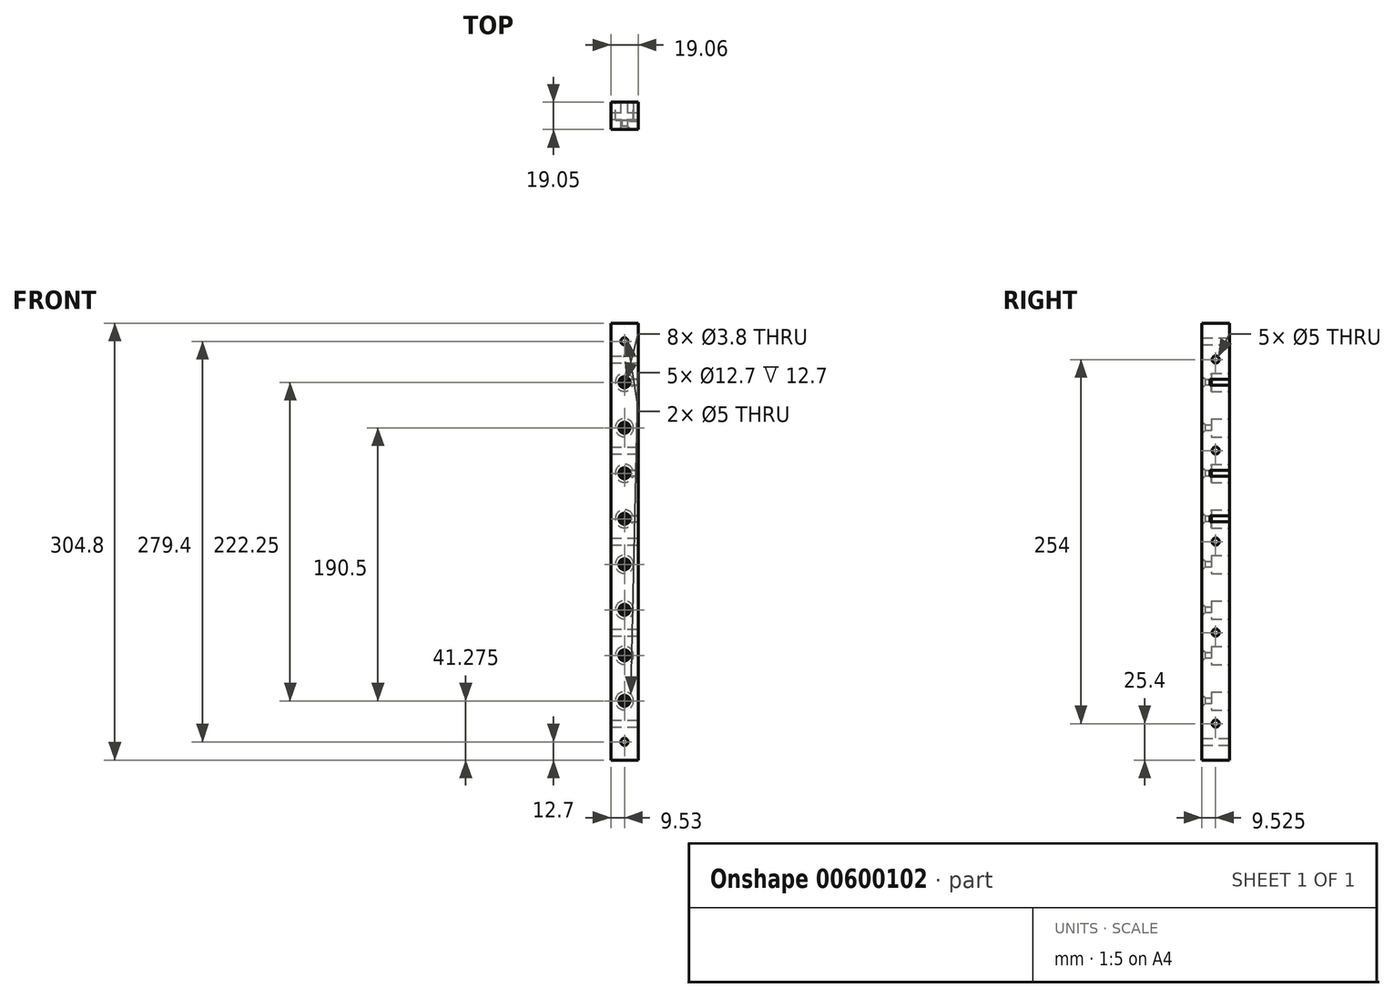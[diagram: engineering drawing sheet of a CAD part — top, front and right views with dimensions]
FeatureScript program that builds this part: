
annotation { "Feature Type Name" : "Feature", "Feature Type Description" : "" }
export const myFeature = defineFeature(function(context is Context, id is Id, definition is map)
    precondition{}
    {
        {
            var Q0;
            Q0=qCreatedBy(makeId("Front.planeOp"),FACE);
            var sketch = newSketch(context, id + "F0", { "sketchPlane" : qUnion([Q0])});
            skLineSegment(sketch, "E0.bottom", {"start": v(-9.52, 152.4) * mm, "end": v(9.53, 152.4) * mm});
            skLineSegment(sketch, "E0.top", {"start": v(-9.53, -152.4) * mm, "end": v(9.52, -152.4) * mm});
            skLineSegment(sketch, "E0.left", {"start": v(-9.52, 152.4) * mm, "end": v(-9.53, -152.4) * mm});
            skLineSegment(sketch, "E0.right", {"start": v(9.53, 152.4) * mm, "end": v(9.52, -152.4) * mm});
            skPoint(sketch, "E0.middle", {"position": v(0, 0) * mm});
            skPoint(sketch, "E1", {"position": v(0, 15.88) * mm});
            skPoint(sketch, "E2", {"position": v(0, -15.88) * mm});
            skPoint(sketch, "E3", {"position": v(0, -47.62) * mm});
            skPoint(sketch, "E4", {"position": v(0, -79.38) * mm});
            skPoint(sketch, "E5", {"position": v(0, -111.12) * mm});
            skPoint(sketch, "E6", {"position": v(0, 47.62) * mm});
            skPoint(sketch, "E7", {"position": v(0, 79.38) * mm});
            skPoint(sketch, "E8", {"position": v(0, 111.12) * mm});
            skSolve(sketch);
        }
        {
            var Q0;
            Q0=makeQuery(id+"F0.imprint","IMPRINT",FACE,{"disambiguationData":[TD([[makeQuery(id+"F0.imprint","IMPRINT",EDGE,{"derivedFrom":sQuery(id+"F0.wireOp",EDGE,"E0.bottom")}),-1.0]])]});
            extrude(context, id + "F1", {"entities" : qUnion([Q0]), "oppositeDirection" : true, "depth" : 19.05 * mm, "offsetDistance" : 25.4 * mm});
        }
        {
            var Q0;
            Q0=makeQuery(id+"F1.opExtrude","SWEPT_FACE",FACE,{"disambiguationData":[OSD([sQuery(id+"F0.wireOp",EDGE,"E0.right")])]});
            var sketch = newSketch(context, id + "F2", { "sketchPlane" : qUnion([Q0])});
            skPoint(sketch, "E9", {"position": v(9.52, 0) * mm});
            skPoint(sketch, "E10", {"position": v(9.53, -63.5) * mm});
            skPoint(sketch, "E11", {"position": v(9.52, 63.5) * mm});
            skPoint(sketch, "E12", {"position": v(9.52, 127) * mm});
            skPoint(sketch, "E13", {"position": v(9.53, -127) * mm});
            skSolve(sketch);
        }
        {
            var Q0;
            Q0=sQuery(id+"F2.wireOp",VERTEX,"E12");
            var Q1;
            Q1=sQuery(id+"F2.wireOp",VERTEX,"E11");
            var Q2;
            Q2=sQuery(id+"F2.wireOp",VERTEX,"E9");
            var Q3;
            Q3=sQuery(id+"F2.wireOp",VERTEX,"E10");
            var Q4;
            Q4=sQuery(id+"F2.wireOp",VERTEX,"E13");
            var Q5;
            Q5=makeQuery(id+"F1.opExtrude","SWEPT_BODY",BODY,{"disambiguationData":[OSD([sQuery(id+"F0.wireOp",EDGE,"E0.bottom"),sQuery(id+"F0.wireOp",EDGE,"E0.top"),sQuery(id+"F0.wireOp",EDGE,"E0.left"),sQuery(id+"F0.wireOp",EDGE,"E0.right")])]});
            hole(context, id + "F3", {"style" : HoleStyle.SIMPLE, "endStyle" : HoleEndStyle.THROUGH, "standardTappedOrClearance" : lookupTablePath({ "standard" : "ISO", "engagement" : "75%", "pitch" : "1 mm", "size" : "M6", "type" : "Tapped" }), "standardBlindInLast" : lookupTablePath({ "standard" : "ISO", "engagement" : "75%", "pitch" : "1 mm", "size" : "M6", "type" : "Tapped" }), "holeDiameter" : 5 * mm, "majorDiameter" : 6 * mm, "showTappedDepth" : true, "isTappedThrough" : true, "tappedDepth" : 12.7 * mm, "tapClearance" : 3, "locations" : qUnion([Q0, Q1, Q2, Q3, Q4]), "scope" : qUnion([Q5])});
        }
        {
            var Q0;
            Q0=makeQuery(id+"F1.opExtrude","CAP_FACE",FACE,{"disambiguationData":[OSD([sQuery(id+"F0.wireOp",EDGE,"E0.bottom"),sQuery(id+"F0.wireOp",EDGE,"E0.top"),sQuery(id+"F0.wireOp",EDGE,"E0.left"),sQuery(id+"F0.wireOp",EDGE,"E0.right")])],"isStart":false});
            var sketch = newSketch(context, id + "F4", { "sketchPlane" : qUnion([Q0])});
            skPoint(sketch, "E14", {"position": v(0, 15.88) * mm});
            skPoint(sketch, "E15", {"position": v(0, 47.62) * mm});
            skPoint(sketch, "E16", {"position": v(0, 79.38) * mm});
            skPoint(sketch, "E17", {"position": v(0, 111.12) * mm});
            skPoint(sketch, "E18", {"position": v(0, -15.88) * mm});
            skPoint(sketch, "E19", {"position": v(0, -47.62) * mm});
            skPoint(sketch, "E20", {"position": v(0, -79.38) * mm});
            skPoint(sketch, "E21", {"position": v(0, -111.12) * mm});
            skCircle(sketch, "E22", {"center": v(0, 111.12) * mm, "radius": 6.35 * mm});
            skCircle(sketch, "E23", {"center": v(0, 79.38) * mm, "radius": 6.35 * mm});
            skCircle(sketch, "E24", {"center": v(0, 47.62) * mm, "radius": 6.35 * mm});
            skCircle(sketch, "E25", {"center": v(0, 15.88) * mm, "radius": 6.35 * mm});
            skCircle(sketch, "E26", {"center": v(0, -111.12) * mm, "radius": 6.35 * mm});
            skCircle(sketch, "E27", {"center": v(0, -79.38) * mm, "radius": 6.35 * mm});
            skCircle(sketch, "E28", {"center": v(0, -47.62) * mm, "radius": 6.35 * mm});
            skCircle(sketch, "E29", {"center": v(0, -15.88) * mm, "radius": 6.35 * mm});
            skSolve(sketch);
        }
        {
            var Q0;
            Q0=sQuery(id+"F0.wireOp",VERTEX,"E8");
            var Q1;
            Q1=sQuery(id+"F0.wireOp",VERTEX,"E7");
            var Q2;
            Q2=sQuery(id+"F0.wireOp",VERTEX,"E6");
            var Q3;
            Q3=sQuery(id+"F0.wireOp",VERTEX,"E1");
            var Q4;
            Q4=sQuery(id+"F0.wireOp",VERTEX,"E2");
            var Q5;
            Q5=sQuery(id+"F0.wireOp",VERTEX,"E3");
            var Q6;
            Q6=sQuery(id+"F0.wireOp",VERTEX,"E4");
            var Q7;
            Q7=sQuery(id+"F0.wireOp",VERTEX,"E5");
            var Q8;
            Q8=makeQuery(id+"F1.opExtrude","SWEPT_BODY",BODY,{"disambiguationData":[OSD([sQuery(id+"F0.wireOp",EDGE,"E0.bottom"),sQuery(id+"F0.wireOp",EDGE,"E0.top"),sQuery(id+"F0.wireOp",EDGE,"E0.left"),sQuery(id+"F0.wireOp",EDGE,"E0.right")])]});
            hole(context, id + "F5", {"style" : HoleStyle.C_SINK, "endStyle" : HoleEndStyle.BLIND, "standardTappedOrClearance" : lookupTablePath({ "standard" : "ANSI", "fit" : "Normal (ASME)", "size" : "#6", "type" : "Clearance" }), "standardBlindInLast" : lookupTablePath({ "fit" : "Free", "standard" : "ANSI", "size" : "#6", "type" : "Clearance" }), "holeDiameter" : 3.8 * mm, "cSinkDiameter" : 7.8 * mm, "cSinkAngle" : 82 * degree, "majorDiameter" : 6.35 * mm, "holeDepth" : 12.7 * mm, "isTappedThrough" : true, "tappedDepth" : 12.7 * mm, "tapClearance" : 3, "locations" : qUnion([Q0, Q1, Q2, Q3, Q4, Q5, Q6, Q7]), "scope" : qUnion([Q8])});
        }
        {
            var Q0;
            Q0=makeQuery(id+"F1.opExtrude","SWEPT_FACE",FACE,{"disambiguationData":[OSD([sQuery(id+"F0.wireOp",EDGE,"E0.right")])]});
            var sketch = newSketch(context, id + "F6", { "sketchPlane" : qUnion([Q0])});
            skPoint(sketch, "E30", {"position": v(19.05, 15.88) * mm});
            skLineSegment(sketch, "E31", {"start": v(5.72, 10.75) * mm, "end": v(5.72, 17.87) * mm});
            skLineSegment(sketch, "E32", {"start": v(5.71, 113.12) * mm, "end": v(5.71, 109.12) * mm});
            skPoint(sketch, "E33", {"position": v(19.05, 47.62) * mm});
            skPoint(sketch, "E34", {"position": v(19.05, 79.38) * mm});
            skPoint(sketch, "E35", {"position": v(19.05, 111.12) * mm});
            skPoint(sketch, "E36", {"position": v(19.05, -15.88) * mm});
            skPoint(sketch, "E37", {"position": v(19.05, -47.62) * mm});
            skPoint(sketch, "E38", {"position": v(19.05, -79.38) * mm});
            skPoint(sketch, "E39", {"position": v(19.05, -111.12) * mm});
            skLineSegment(sketch, "E40.0", {"start": v(20, 113.12) * mm, "end": v(5.71, 113.12) * mm});
            skLineSegment(sketch, "E41.0", {"start": v(20, 109.12) * mm, "end": v(5.71, 109.12) * mm});
            skLineSegment(sketch, "E42.0", {"start": v(-6.35, 158.75) * mm, "end": v(-6.35, -158.75) * mm});
            skLineSegment(sketch, "E42.1", {"start": v(25.4, 158.75) * mm, "end": v(-6.35, 158.75) * mm});
            skLineSegment(sketch, "E42.2", {"start": v(25.4, -158.75) * mm, "end": v(25.4, 158.75) * mm});
            skLineSegment(sketch, "E42.3", {"start": v(-6.35, -158.75) * mm, "end": v(25.4, -158.75) * mm});
            skLineSegment(sketch, "E43", {"start": v(20, 113.12) * mm, "end": v(20, 109.12) * mm});
            skLineSegment(sketch, "E44.0", {"start": v(20, 81.38) * mm, "end": v(5.72, 81.38) * mm});
            skLineSegment(sketch, "E45.0", {"start": v(20, 77.38) * mm, "end": v(5.72, 77.38) * mm});
            skLineSegment(sketch, "E46", {"start": v(5.72, 81.38) * mm, "end": v(5.72, 77.38) * mm});
            skLineSegment(sketch, "E47", {"start": v(5.83, 77.47) * mm, "end": v(20, 77.38) * mm});
            skLineSegment(sketch, "E48", {"start": v(20, 81.38) * mm, "end": v(20, 77.38) * mm});
            skLineSegment(sketch, "E49.0", {"start": v(20, 49.62) * mm, "end": v(5.72, 49.62) * mm});
            skLineSegment(sketch, "E50.0", {"start": v(20, 45.62) * mm, "end": v(5.72, 45.62) * mm});
            skLineSegment(sketch, "E51", {"start": v(5.72, 49.62) * mm, "end": v(5.72, 45.62) * mm});
            skLineSegment(sketch, "E52", {"start": v(20, 49.62) * mm, "end": v(20, 45.62) * mm});
            skLineSegment(sketch, "E53.0", {"start": v(20, 17.87) * mm, "end": v(5.71, 17.87) * mm});
            skLineSegment(sketch, "E54.0", {"start": v(20, 13.87) * mm, "end": v(5.71, 13.87) * mm});
            skLineSegment(sketch, "E55", {"start": v(5.71, 17.87) * mm, "end": v(5.71, 13.87) * mm});
            skLineSegment(sketch, "E56", {"start": v(5.67, 13.88) * mm, "end": v(20, 13.87) * mm});
            skLineSegment(sketch, "E57", {"start": v(20, 17.87) * mm, "end": v(20, 13.87) * mm});
            skLineSegment(sketch, "E58.0", {"start": v(20, -17.88) * mm, "end": v(5.72, -17.88) * mm});
            skLineSegment(sketch, "E59.0", {"start": v(20, -13.88) * mm, "end": v(5.72, -13.88) * mm});
            skLineSegment(sketch, "E60.0", {"start": v(-2, 154.4) * mm, "end": v(-2, -154.4) * mm});
            skLineSegment(sketch, "E60.1", {"start": v(21.05, 154.4) * mm, "end": v(-2, 154.4) * mm});
            skLineSegment(sketch, "E60.2", {"start": v(21.05, -154.4) * mm, "end": v(21.05, 154.4) * mm});
            skLineSegment(sketch, "E60.3", {"start": v(-2, -154.4) * mm, "end": v(21.05, -154.4) * mm});
            skLineSegment(sketch, "E61.bottom", {"start": v(5.72, -13.88) * mm, "end": v(20, -13.88) * mm});
            skLineSegment(sketch, "E61.top", {"start": v(5.72, -17.88) * mm, "end": v(20, -17.88) * mm});
            skLineSegment(sketch, "E61.left", {"start": v(5.72, -13.88) * mm, "end": v(5.72, -17.88) * mm});
            skLineSegment(sketch, "E61.right", {"start": v(20, -13.88) * mm, "end": v(20, -17.88) * mm});
            skLineSegment(sketch, "E62.0", {"start": v(20, -45.63) * mm, "end": v(5.72, -45.63) * mm});
            skLineSegment(sketch, "E63.0", {"start": v(20, -49.63) * mm, "end": v(5.72, -49.63) * mm});
            skLineSegment(sketch, "E64.bottom", {"start": v(5.72, -45.63) * mm, "end": v(20, -45.63) * mm});
            skLineSegment(sketch, "E64.top", {"start": v(5.72, -49.63) * mm, "end": v(20, -49.63) * mm});
            skLineSegment(sketch, "E64.left", {"start": v(5.72, -45.63) * mm, "end": v(5.72, -49.63) * mm});
            skLineSegment(sketch, "E64.right", {"start": v(20, -45.63) * mm, "end": v(20, -49.63) * mm});
            skLineSegment(sketch, "E65.0", {"start": v(20, -77.38) * mm, "end": v(5.72, -77.38) * mm});
            skLineSegment(sketch, "E66.0", {"start": v(20, -81.38) * mm, "end": v(5.72, -81.38) * mm});
            skLineSegment(sketch, "E67.bottom", {"start": v(5.72, -77.38) * mm, "end": v(20, -77.38) * mm});
            skLineSegment(sketch, "E67.top", {"start": v(5.72, -81.38) * mm, "end": v(20, -81.38) * mm});
            skLineSegment(sketch, "E67.left", {"start": v(5.72, -77.38) * mm, "end": v(5.72, -81.38) * mm});
            skLineSegment(sketch, "E67.right", {"start": v(20, -77.38) * mm, "end": v(20, -81.38) * mm});
            skLineSegment(sketch, "E68.0", {"start": v(20, -109.13) * mm, "end": v(5.72, -109.13) * mm});
            skLineSegment(sketch, "E69.0", {"start": v(20, -113.12) * mm, "end": v(5.72, -113.12) * mm});
            skLineSegment(sketch, "E70.bottom", {"start": v(5.72, -109.13) * mm, "end": v(20, -109.13) * mm});
            skLineSegment(sketch, "E70.top", {"start": v(5.72, -113.12) * mm, "end": v(20, -113.12) * mm});
            skLineSegment(sketch, "E70.left", {"start": v(5.72, -109.13) * mm, "end": v(5.72, -113.12) * mm});
            skLineSegment(sketch, "E70.right", {"start": v(20, -109.13) * mm, "end": v(20, -113.12) * mm});
            skPoint(sketch, "E71.orphan", {"position": v(5.72, -152.4) * mm});
            skLineSegment(sketch, "E72.trimOffspring", {"start": v(5.71, 81.38) * mm, "end": v(5.71, 77.38) * mm});
            skLineSegment(sketch, "E73.trimOffspring", {"start": v(5.71, 109.12) * mm, "end": v(5.71, 113.12) * mm});
            skLineSegment(sketch, "E74.trimOffspring", {"start": v(5.71, 49.62) * mm, "end": v(5.71, 45.62) * mm});
            skLineSegment(sketch, "E75.trimOffspring", {"start": v(5.72, 77.38) * mm, "end": v(5.72, 81.38) * mm});
            skLineSegment(sketch, "E76.trimOffspring", {"start": v(5.72, 45.62) * mm, "end": v(5.72, 49.62) * mm});
            skSolve(sketch);
        }
        {
            var Q0;
            Q0 = qSketchRegion(id + "F6", true);
            var Q1;
            Q1=makeQuery(id+"F6.imprint","IMPRINT",FACE,{"disambiguationData":[TD([[makeQuery(id+"F6.imprint","IMPRINT",EDGE,{"derivedFrom":sQuery(id+"F6.wireOp",EDGE,"E40.0")}),1.0]])]});
            var Q2;
            Q2=makeQuery(id+"F6.imprint","IMPRINT",FACE,{"disambiguationData":[TD([[makeQuery(id+"F6.imprint","IMPRINT",EDGE,{"derivedFrom":sQuery(id+"F6.wireOp",EDGE,"E44.0")}),1.0]])]});
            var Q3;
            Q3=makeQuery(id+"F6.imprint","IMPRINT",FACE,{"disambiguationData":[TD([[makeQuery(id+"F6.imprint","IMPRINT",EDGE,{"derivedFrom":sQuery(id+"F6.wireOp",EDGE,"E49.0")}),1.0]])]});
            var Q4;
            {var subQ2=sQuery(id+"F6.wireOp",EDGE,"E53.0");Q4=makeQuery(id+"F6.imprint","IMPRINT",FACE,{"disambiguationData":[TD([[makeQuery(id+"F6.imprint","IMPRINT",EDGE,{"derivedFrom":subQ2}),1.0]])]});}
            var Q5;
            Q5=makeQuery(id+"F6.imprint","IMPRINT",FACE,{"disambiguationData":[TD([[makeQuery(id+"F6.imprint","IMPRINT",EDGE,{"derivedFrom":sQuery(id+"F6.wireOp",EDGE,"E61.bottom")}),-1.0]])]});
            var Q6;
            Q6=makeQuery(id+"F6.imprint","IMPRINT",FACE,{"disambiguationData":[TD([[makeQuery(id+"F6.imprint","IMPRINT",EDGE,{"derivedFrom":sQuery(id+"F6.wireOp",EDGE,"E64.bottom")}),-1.0]])]});
            var Q7;
            Q7=makeQuery(id+"F6.imprint","IMPRINT",FACE,{"disambiguationData":[TD([[makeQuery(id+"F6.imprint","IMPRINT",EDGE,{"derivedFrom":sQuery(id+"F6.wireOp",EDGE,"E67.bottom")}),-1.0]])]});
            var Q8;
            Q8=makeQuery(id+"F6.imprint","IMPRINT",FACE,{"disambiguationData":[TD([[makeQuery(id+"F6.imprint","IMPRINT",EDGE,{"derivedFrom":sQuery(id+"F6.wireOp",EDGE,"E70.bottom")}),-1.0]])]});
            var Q9;
            {var subQ0=sQuery(id+"F6.wireOp",EDGE,"E75.trimOffspring");Q9=makeQuery(id+"F6.imprint","IMPRINT",FACE,{"disambiguationData":[TD([[makeQuery(id+"F6.imprint","IMPRINT",EDGE,{"derivedFrom":subQ0}),-1.0]])]});}
            extrude(context, id + "F7", {"entities" : qUnion([Q0, Q1, Q2, Q3, Q4, Q5, Q6, Q7, Q8, Q9]), "operationType" : NewBodyOperationType.REMOVE, "oppositeDirection" : true, "depth" : 6.35 * mm, "offsetDistance" : 25.4 * mm});
        }
        {
            var Q0;
            Q0=makeQuery(id+"F4.imprint","IMPRINT",FACE,{"disambiguationData":[TD([[makeQuery(id+"F4.imprint","IMPRINT",EDGE,{"derivedFrom":sQuery(id+"F4.wireOp",EDGE,"E22")}),1.0]])]});
            var Q1;
            Q1=makeQuery(id+"F4.imprint","IMPRINT",FACE,{"disambiguationData":[TD([[makeQuery(id+"F4.imprint","IMPRINT",EDGE,{"derivedFrom":sQuery(id+"F4.wireOp",EDGE,"E23")}),1.0]])]});
            var Q2;
            Q2=makeQuery(id+"F4.imprint","IMPRINT",FACE,{"disambiguationData":[TD([[makeQuery(id+"F4.imprint","IMPRINT",EDGE,{"derivedFrom":sQuery(id+"F4.wireOp",EDGE,"E24")}),1.0]])]});
            var Q3;
            Q3=makeQuery(id+"F4.imprint","IMPRINT",FACE,{"disambiguationData":[TD([[makeQuery(id+"F4.imprint","IMPRINT",EDGE,{"derivedFrom":sQuery(id+"F4.wireOp",EDGE,"E25")}),1.0]])]});
            var Q4;
            Q4=makeQuery(id+"F4.imprint","IMPRINT",FACE,{"disambiguationData":[TD([[makeQuery(id+"F4.imprint","IMPRINT",EDGE,{"derivedFrom":sQuery(id+"F4.wireOp",EDGE,"E28")}),1.0]])]});
            var Q5;
            Q5=makeQuery(id+"F4.imprint","IMPRINT",FACE,{"disambiguationData":[TD([[makeQuery(id+"F4.imprint","IMPRINT",EDGE,{"derivedFrom":sQuery(id+"F4.wireOp",EDGE,"E27")}),1.0]])]});
            var Q6;
            Q6=makeQuery(id+"F4.imprint","IMPRINT",FACE,{"disambiguationData":[TD([[makeQuery(id+"F4.imprint","IMPRINT",EDGE,{"derivedFrom":sQuery(id+"F4.wireOp",EDGE,"E26")}),1.0]])]});
            var Q7;
            Q7=makeQuery(id+"F4.imprint","IMPRINT",FACE,{"disambiguationData":[TD([[makeQuery(id+"F4.imprint","IMPRINT",EDGE,{"derivedFrom":sQuery(id+"F4.wireOp",EDGE,"E29")}),1.0]])]});
            extrude(context, id + "F8", {"entities" : qUnion([Q0, Q1, Q2, Q3, Q4, Q5, Q6, Q7]), "operationType" : NewBodyOperationType.REMOVE, "oppositeDirection" : true, "depth" : 12.7 * mm, "offsetDistance" : 25.4 * mm});
        }
        {
            var Q0;
            Q0=makeQuery(id+"F1.opExtrude","CAP_FACE",FACE,{"disambiguationData":[OSD([sQuery(id+"F0.wireOp",EDGE,"E0.bottom"),sQuery(id+"F0.wireOp",EDGE,"E0.top"),sQuery(id+"F0.wireOp",EDGE,"E0.left"),sQuery(id+"F0.wireOp",EDGE,"E0.right")])],"isStart":false});
            var sketch = newSketch(context, id + "F9", { "sketchPlane" : qUnion([Q0])});
            skPoint(sketch, "E77", {"position": v(0, -139.7) * mm});
            skPoint(sketch, "E78", {"position": v(0, 139.7) * mm});
            skSolve(sketch);
        }
        {
            var Q0;
            Q0=sQuery(id+"F9.wireOp",VERTEX,"E78");
            var Q1;
            Q1=sQuery(id+"F9.wireOp",VERTEX,"E77");
            var Q2;
            Q2=makeQuery(id+"F1.opExtrude","SWEPT_BODY",BODY,{"disambiguationData":[OSD([sQuery(id+"F0.wireOp",EDGE,"E0.bottom"),sQuery(id+"F0.wireOp",EDGE,"E0.top"),sQuery(id+"F0.wireOp",EDGE,"E0.left"),sQuery(id+"F0.wireOp",EDGE,"E0.right")])]});
            hole(context, id + "F10", {"style" : HoleStyle.SIMPLE, "endStyle" : HoleEndStyle.THROUGH, "standardTappedOrClearance" : lookupTablePath({ "standard" : "ISO", "engagement" : "75%", "pitch" : "1 mm", "size" : "M6", "type" : "Tapped" }), "standardBlindInLast" : lookupTablePath({ "standard" : "ISO", "engagement" : "75%", "pitch" : "1 mm", "size" : "M6", "type" : "Tapped" }), "holeDiameter" : 5 * mm, "majorDiameter" : 6 * mm, "showTappedDepth" : true, "isTappedThrough" : true, "tappedDepth" : 12.7 * mm, "tapClearance" : 3, "locations" : qUnion([Q0, Q1]), "scope" : qUnion([Q2])});
        }
    });
